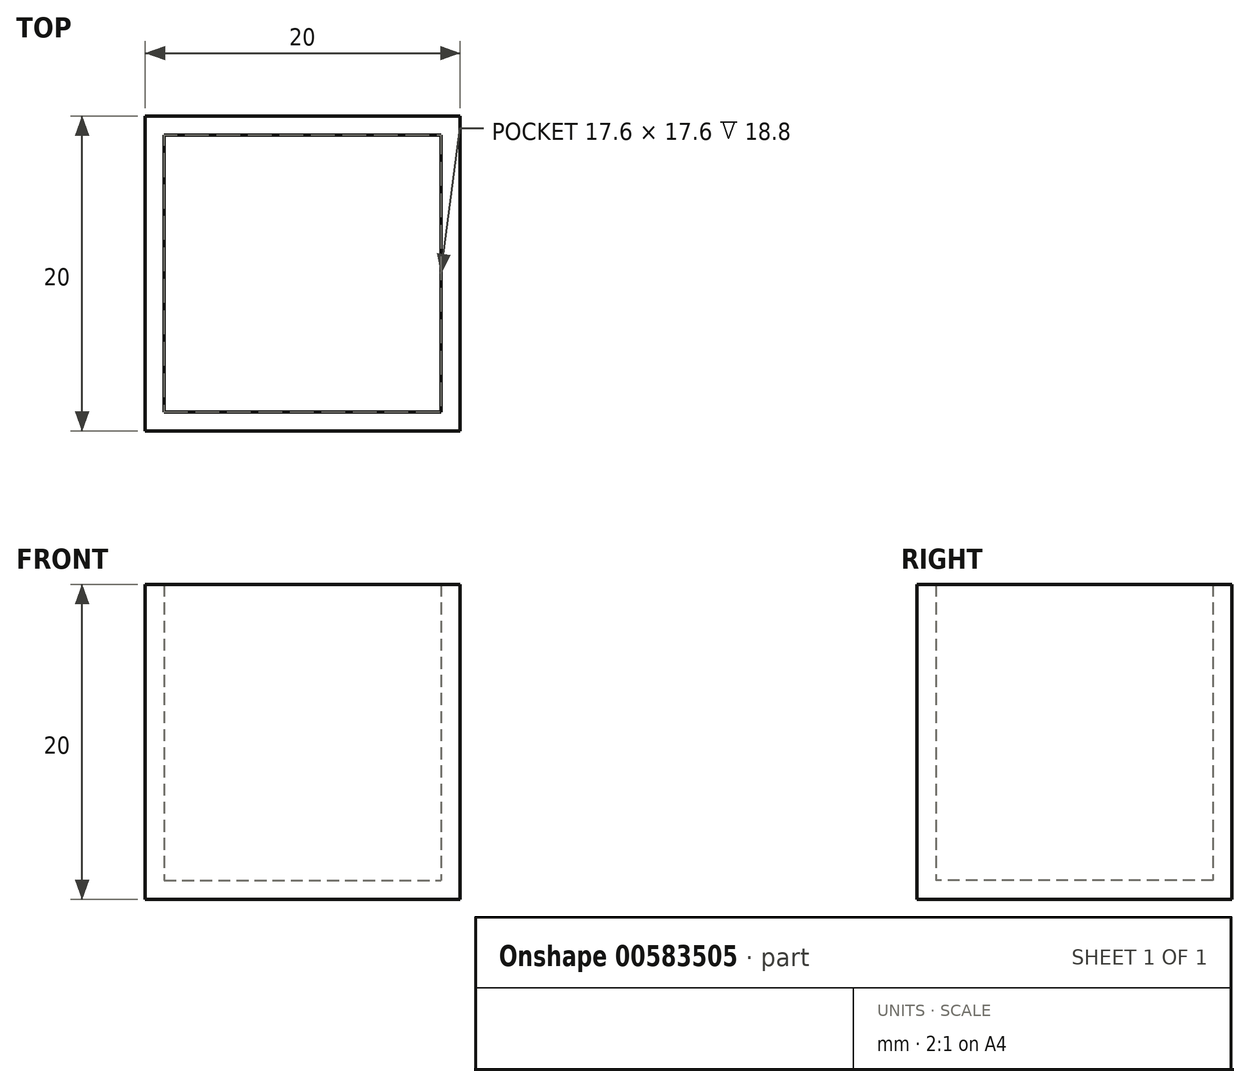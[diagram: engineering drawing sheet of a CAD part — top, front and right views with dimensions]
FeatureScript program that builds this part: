
annotation { "Feature Type Name" : "Feature", "Feature Type Description" : "" }
export const myFeature = defineFeature(function(context is Context, id is Id, definition is map)
    precondition{}
    {
        {
            var Q0;
            Q0=qCreatedBy(makeId("Top.planeOp"),FACE);
            var sketch = newSketch(context, id + "F0", { "sketchPlane" : qUnion([Q0])});
            skLineSegment(sketch, "E0.bottom", {"start": v(-10, 10) * mm, "end": v(10, 10) * mm});
            skLineSegment(sketch, "E0.top", {"start": v(-10, -10) * mm, "end": v(10, -10) * mm});
            skLineSegment(sketch, "E0.left", {"start": v(-10, 10) * mm, "end": v(-10, -10) * mm});
            skLineSegment(sketch, "E0.right", {"start": v(10, 10) * mm, "end": v(10, -10) * mm});
            skLineSegment(sketch, "E1.0", {"start": v(-8.8, 8.8) * mm, "end": v(8.8, 8.8) * mm});
            skLineSegment(sketch, "E1.1", {"start": v(-8.8, 8.8) * mm, "end": v(-8.8, -8.8) * mm});
            skLineSegment(sketch, "E1.2", {"start": v(-8.8, -8.8) * mm, "end": v(8.8, -8.8) * mm});
            skLineSegment(sketch, "E1.3", {"start": v(8.8, 8.8) * mm, "end": v(8.8, -8.8) * mm});
            skSolve(sketch);
        }
        {
            var Q0;
            Q0 = qSketchRegion(id + "F0", true);
            extrude(context, id + "F1", {"entities" : qUnion([Q0]), "depth" : 20 * mm, "offsetDistance" : 25 * mm});
        }
        {
            var Q0;
            Q0=makeQuery(id+"F0.imprint","IMPRINT",FACE,{"disambiguationData":[TD([[makeQuery(id+"F0.imprint","IMPRINT",EDGE,{"derivedFrom":sQuery(id+"F0.wireOp",EDGE,"E1.0")}),-1.0]])]});
            extrude(context, id + "F2", {"entities" : qUnion([Q0]), "operationType" : NewBodyOperationType.ADD, "depth" : 1.2 * mm, "offsetDistance" : 25 * mm});
        }
    });
